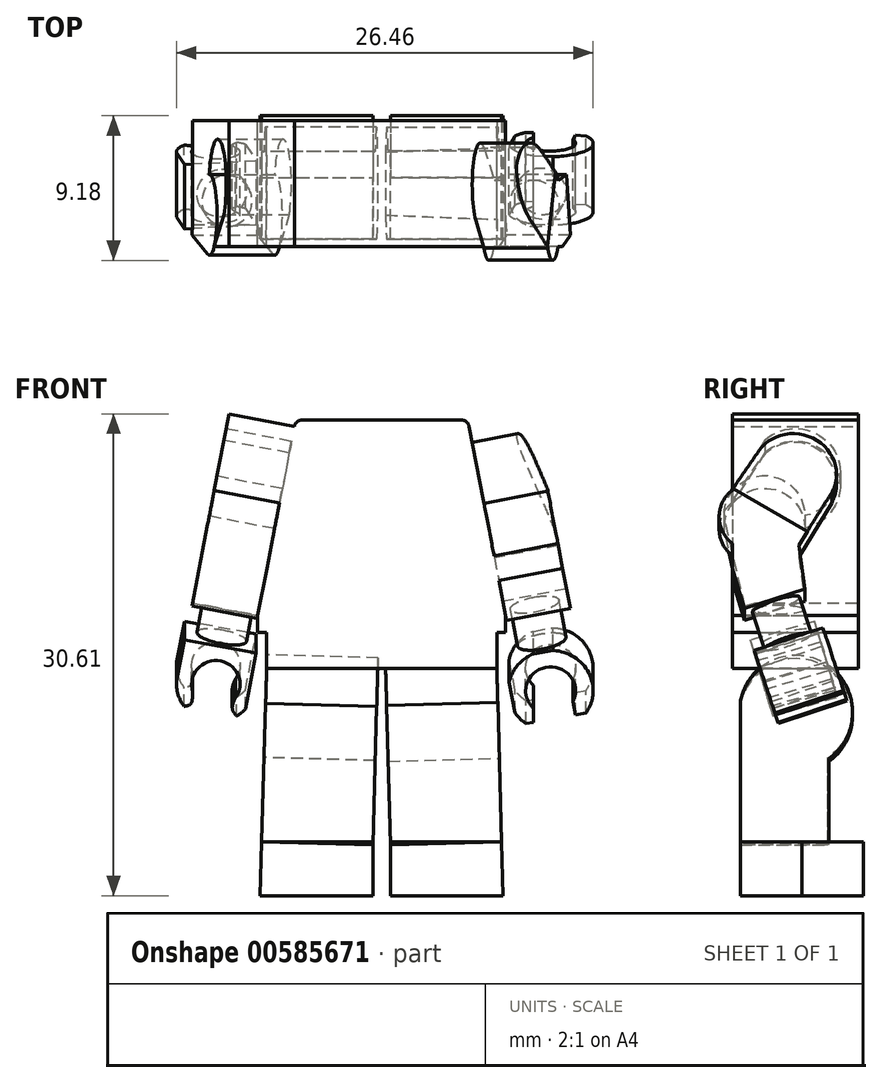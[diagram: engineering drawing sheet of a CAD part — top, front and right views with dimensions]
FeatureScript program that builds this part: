
annotation { "Feature Type Name" : "Feature", "Feature Type Description" : "" }
export const myFeature = defineFeature(function(context is Context, id is Id, definition is map)
    precondition{}
    {
        {
            var Q0;
            Q0=qCreatedBy(makeId("Front.planeOp"),FACE);
            var sketch = newSketch(context, id + "F0", { "sketchPlane" : qUnion([Q0])});
            skLineSegment(sketch, "E0", {"start": v(0, 25.85) * mm, "end": v(-2.45, 25.85) * mm});
            skLineSegment(sketch, "E1", {"start": v(-2.45, 25.85) * mm, "end": v(-2.45, 23.62) * mm});
            skLineSegment(sketch, "E2", {"start": v(-2.45, 23.62) * mm, "end": v(-3.1, 23.62) * mm});
            skLineSegment(sketch, "E3", {"start": v(-5.1, 21.62) * mm, "end": v(-5.1, 17.12) * mm});
            skLineSegment(sketch, "E4", {"start": v(-3.1, 15.12) * mm, "end": v(0, 15.12) * mm});
            skLineSegment(sketch, "E5", {"start": v(0, 25.85) * mm, "end": v(0, 15.12) * mm, "construction": true});
            skPoint(sketch, "E6.visualSharp", {"position": v(-5.1, 23.62) * mm});
            skArc(sketch, "E6.filletArc", {"start": v(-3.1, 23.62) * mm, "mid": v(-4.51, 23.03) * mm, "end": v(-5.1, 21.62) * mm});
            skPoint(sketch, "E7.visualSharp", {"position": v(-5.1, 15.12) * mm});
            skArc(sketch, "E7.filletArc", {"start": v(-5.1, 17.12) * mm, "mid": v(-4.51, 15.7) * mm, "end": v(-3.1, 15.12) * mm});
            skLineSegment(sketch, "E8", {"start": v(-3.1, 15.12) * mm, "end": v(-3.1, 14.02) * mm});
            skLineSegment(sketch, "E9", {"start": v(-3.1, 14.02) * mm, "end": v(0, 14.02) * mm});
            skLineSegment(sketch, "E10", {"start": v(0, 15.12) * mm, "end": v(0, 14.02) * mm, "construction": true});
            skLineSegment(sketch, "E11", {"start": v(0, 14.02) * mm, "end": v(-5.06, 14.02) * mm});
            skPoint(sketch, "E11.endSnap0", {"position": v(-1.55, 14.02) * mm});
            skLineSegment(sketch, "E12", {"start": v(-5.55, 13.62) * mm, "end": v(-7.87, 1.6) * mm});
            skLineSegment(sketch, "E13", {"start": v(-7.87, 1.6) * mm, "end": v(0, 1.6) * mm});
            skLineSegment(sketch, "E14", {"start": v(0, 14.02) * mm, "end": v(0, 1.6) * mm, "construction": true});
            skLineSegment(sketch, "E15.MirrorCS", {"start": v(5.55, 13.62) * mm, "end": v(7.87, 1.6) * mm});
            skLineSegment(sketch, "E16.MirrorCS", {"start": v(7.87, 1.6) * mm, "end": v(0, 1.6) * mm});
            skLineSegment(sketch, "E17.MirrorCS", {"start": v(0, 14.02) * mm, "end": v(5.06, 14.02) * mm});
            skLineSegment(sketch, "E18", {"start": v(-7.87, 1.6) * mm, "end": v(-7.87, 0.52) * mm});
            skLineSegment(sketch, "E19", {"start": v(-7.87, 0.52) * mm, "end": v(0, 0.52) * mm});
            skLineSegment(sketch, "E20", {"start": v(0, -31.62) * mm, "end": v(0, 1.6) * mm, "construction": true});
            skLineSegment(sketch, "E21", {"start": v(-7.3, 0.52) * mm, "end": v(-7.3, -1.76) * mm});
            skLineSegment(sketch, "E22", {"start": v(-7.3, -1.76) * mm, "end": v(0, -1.76) * mm});
            skLineSegment(sketch, "E23", {"start": v(-7.3, -1.76) * mm, "end": v(-7.72, -16.2) * mm});
            skLineSegment(sketch, "E24", {"start": v(-7.72, -16.2) * mm, "end": v(-0.56, -16.2) * mm});
            skLineSegment(sketch, "E25", {"start": v(-0.56, -16.2) * mm, "end": v(-0.56, -8.11) * mm});
            skLineSegment(sketch, "E26", {"start": v(-0.56, -8.11) * mm, "end": v(-0.85, -8.11) * mm});
            skLineSegment(sketch, "E27", {"start": v(-0.85, -8.11) * mm, "end": v(-0.85, -4.94) * mm});
            skLineSegment(sketch, "E28", {"start": v(-0.56, -8.11) * mm, "end": v(0, -8.11) * mm});
            skLineSegment(sketch, "E29.MirrorCS", {"start": v(7.87, 1.6) * mm, "end": v(7.87, 0.52) * mm});
            skLineSegment(sketch, "E30.MirrorCS", {"start": v(7.87, 0.52) * mm, "end": v(0, 0.52) * mm});
            skLineSegment(sketch, "E31.MirrorCS", {"start": v(7.3, -1.76) * mm, "end": v(0, -1.76) * mm});
            skLineSegment(sketch, "E32.MirrorCS", {"start": v(7.3, 0.52) * mm, "end": v(7.3, -1.76) * mm});
            skLineSegment(sketch, "E33.MirrorCS", {"start": v(0.85, -8.11) * mm, "end": v(0.85, -4.94) * mm});
            skLineSegment(sketch, "E34.MirrorCS", {"start": v(0.56, -8.11) * mm, "end": v(0.85, -8.11) * mm});
            skLineSegment(sketch, "E35.MirrorCS", {"start": v(0.56, -8.11) * mm, "end": v(0, -8.11) * mm});
            skLineSegment(sketch, "E36.MirrorCS", {"start": v(0.56, -16.2) * mm, "end": v(0.56, -8.11) * mm});
            skLineSegment(sketch, "E37.MirrorCS", {"start": v(7.72, -16.2) * mm, "end": v(0.56, -16.2) * mm});
            skLineSegment(sketch, "E38.MirrorCS", {"start": v(7.3, -1.76) * mm, "end": v(7.72, -16.2) * mm});
            skLineSegment(sketch, "E39", {"start": v(-7.62, -12.78) * mm, "end": v(-0.56, -12.78) * mm});
            skLineSegment(sketch, "E40", {"start": v(0.56, -12.78) * mm, "end": v(7.62, -12.78) * mm});
            skPoint(sketch, "E41", {"position": v(-0.85, -4.94) * mm});
            skLineSegment(sketch, "E42", {"start": v(-0.85, -4.94) * mm, "end": v(0, -4.94) * mm, "construction": true});
            skLineSegment(sketch, "E43", {"start": v(-0.85, -4.94) * mm, "end": v(-0.85, -1.76) * mm});
            skLineSegment(sketch, "E44", {"start": v(0, -4.94) * mm, "end": v(0.85, -4.94) * mm, "construction": true});
            skPoint(sketch, "E45", {"position": v(0.85, -4.94) * mm});
            skLineSegment(sketch, "E46", {"start": v(0.85, -4.94) * mm, "end": v(0.85, -1.76) * mm});
            skPoint(sketch, "E47.visualSharp", {"position": v(5.47, 14.02) * mm});
            skArc(sketch, "E47.filletArc", {"start": v(5.55, 13.62) * mm, "mid": v(5.38, 13.91) * mm, "end": v(5.06, 14.02) * mm});
            skPoint(sketch, "E48.visualSharp", {"position": v(-5.47, 14.02) * mm});
            skArc(sketch, "E48.filletArc", {"start": v(-5.06, 14.02) * mm, "mid": v(-5.38, 13.91) * mm, "end": v(-5.55, 13.62) * mm});
            skSolve(sketch);
        }
        {
            var Q0;
            Q0=sQuery(id+"F0.wireOp",EDGE,"E0");
            var Q1;
            Q1=sQuery(id+"F0.wireOp",EDGE,"E1");
            var Q2;
            Q2=sQuery(id+"F0.wireOp",EDGE,"E2");
            var Q3;
            Q3=sQuery(id+"F0.wireOp",EDGE,"E6.filletArc");
            var Q4;
            Q4=sQuery(id+"F0.wireOp",EDGE,"E3");
            var Q5;
            Q5=sQuery(id+"F0.wireOp",EDGE,"E7.filletArc");
            var Q6;
            Q6=sQuery(id+"F0.wireOp",EDGE,"E8");
            var Q7;
            Q7=sQuery(id+"F0.wireOp",EDGE,"E9");
            var Q8;
            Q8=sQuery(id+"F0.wireOp",EDGE,"E5");
            revolve(context, id + "F1", {"bodyType" : ToolBodyType.SURFACE, "surfaceEntities" : qUnion([Q0, Q1, Q2, Q3, Q4, Q5, Q6, Q7]), "axis" : qUnion([Q8]), "revolveType" : RevolveType.FULL});
        }
        {
            var Q0;
            {var subQ0=sQuery(id+"F0.wireOp",EDGE,"E24");Q0=makeQuery(id+"F0.imprint","IMPRINT",FACE,{"disambiguationData":[TD([[makeQuery(id+"F0.imprint","IMPRINT",EDGE,{"derivedFrom":subQ0}),1.0]])]});}
            var Q1;
            {var subQ0=sQuery(id+"F0.wireOp",EDGE,"E37.MirrorCS");Q1=makeQuery(id+"F0.imprint","IMPRINT",FACE,{"disambiguationData":[TD([[makeQuery(id+"F0.imprint","IMPRINT",EDGE,{"derivedFrom":subQ0}),-1.0]])]});}
            extrude(context, id + "F2", {"entities" : qUnion([Q0, Q1]), "depth" : 3.92 * mm, "offsetDistance" : 25 * mm});
        }
        {
            var Q0;
            {var subQ0=sQuery(id+"F0.wireOp",EDGE,"E24");Q0=makeQuery(id+"F0.imprint","IMPRINT",FACE,{"disambiguationData":[TD([[makeQuery(id+"F0.imprint","IMPRINT",EDGE,{"derivedFrom":subQ0}),1.0]])]});}
            var Q1;
            {var subQ0=sQuery(id+"F0.wireOp",EDGE,"E37.MirrorCS");Q1=makeQuery(id+"F0.imprint","IMPRINT",FACE,{"disambiguationData":[TD([[makeQuery(id+"F0.imprint","IMPRINT",EDGE,{"derivedFrom":subQ0}),-1.0]])]});}
            extrude(context, id + "F3", {"entities" : qUnion([Q0, Q1]), "oppositeDirection" : true, "depth" : 3.92 * mm, "offsetDistance" : 25 * mm});
        }
        {
            var Q0;
            Q0=makeQuery(id+"F2.opExtrude","SWEPT_FACE",FACE,{"disambiguationData":[OSD([sQuery(id+"F0.wireOp",EDGE,"E38.MirrorCS")])]});
            var sketch = newSketch(context, id + "F4", { "sketchPlane" : qUnion([Q0])});
            skLineSegment(sketch, "E49", {"start": v(-3.92, -12.99) * mm, "end": v(-3.92, -4.1) * mm});
            skLineSegment(sketch, "E50", {"start": v(-3.92, -4.1) * mm, "end": v(1.72, -12.99) * mm});
            skLineSegment(sketch, "E51", {"start": v(1.72, -12.99) * mm, "end": v(1.72, -7.67) * mm});
            skCircle(sketch, "E52", {"center": v(-0.38, -4.75) * mm, "radius": 3.6 * mm});
            skPoint(sketch, "E52.third.point", {"position": v(1.85, -1.94) * mm});
            skLineSegment(sketch, "E53", {"start": v(-3.92, -12.99) * mm, "end": v(1.72, -12.99) * mm});
            skSolve(sketch);
        }
        {
            var Q0;
            {var subQ3=sQuery(id+"F4.wireOp",EDGE,"E49");var subQ5=sQuery(id+"F4.wireOp",EDGE,"E52");var subQ6=makeQuery(id+"F4.imprint","INTERSECT",VERTEX,{"derivedFrom":[subQ3,subQ5]});Q0=makeQuery(id+"F4.imprint","IMPRINT",FACE,{"disambiguationData":[TD([[makeQuery(id+"F4.imprint","IMPRINT",EDGE,{"disambiguationData":[TD([[subQ6,-1.0]])],"derivedFrom":subQ5}),-1.0]])]});}
            var Q1;
            {var subQ0=sQuery(id+"F4.wireOp",EDGE,"E51");Q1=makeQuery(id+"F4.imprint","IMPRINT",FACE,{"disambiguationData":[TD([[makeQuery(id+"F4.imprint","IMPRINT",EDGE,{"derivedFrom":subQ0}),1.0]])]});}
            var Q2;
            {var subQ0=sQuery(id+"F4.wireOp",EDGE,"E52");var subQ2=sQuery(id+"F4.wireOp",EDGE,"E49");var subQ4=makeQuery(id+"F4.imprint","INTERSECT",VERTEX,{"derivedFrom":[subQ2,subQ0]});Q2=makeQuery(id+"F4.imprint","IMPRINT",FACE,{"disambiguationData":[TD([[makeQuery(id+"F4.imprint","IMPRINT",EDGE,{"disambiguationData":[TD([[subQ4,-1.0]])],"derivedFrom":subQ0}),1.0]])]});}
            var Q3;
            {var subQ0=sQuery(id+"F4.wireOp",EDGE,"E52");var subQ4=makeQuery(id+"F4.imprint","INTERSECT",VERTEX,{"derivedFrom":[sQuery(id+"F4.wireOp",EDGE,"E51"),subQ0]});Q3=makeQuery(id+"F4.imprint","IMPRINT",FACE,{"disambiguationData":[TD([[makeQuery(id+"F4.imprint","IMPRINT",EDGE,{"disambiguationData":[TD([[subQ4,1.0]])],"derivedFrom":subQ0}),1.0]])]});}
            extrude(context, id + "F5", {"entities" : qUnion([Q0, Q1, Q2, Q3]), "oppositeDirection" : true, "depth" : 7.06 * mm, "offsetDistance" : 25 * mm});
        }
        {
            var Q0;
            {var subQ0=sQuery(id+"F0.wireOp",EDGE,"E12");Q0=makeQuery(id+"F0.imprint","IMPRINT",FACE,{"disambiguationData":[TD([[makeQuery(id+"F0.imprint","IMPRINT",EDGE,{"derivedFrom":subQ0}),1.0]])]});}
            var Q1;
            Q1=makeQuery(id+"F0.imprint","IMPRINT",FACE,{"disambiguationData":[TD([[makeQuery(id+"F0.imprint","IMPRINT",EDGE,{"derivedFrom":sQuery(id+"F0.wireOp",EDGE,"E13")}),-1.0]])]});
            var Q2;
            {var subQ8=sQuery(id+"F0.wireOp",EDGE,"E21");Q2=makeQuery(id+"F0.imprint","IMPRINT",FACE,{"disambiguationData":[TD([[makeQuery(id+"F0.imprint","IMPRINT",EDGE,{"derivedFrom":subQ8}),1.0]])]});}
            extrude(context, id + "F6", {"entities" : qUnion([Q0, Q1, Q2]), "operationType" : NewBodyOperationType.ADD, "depth" : 4.4 * mm, "offsetDistance" : 25 * mm});
        }
        {
            var Q0;
            {var subQ8=sQuery(id+"F0.wireOp",EDGE,"E21");Q0=makeQuery(id+"F0.imprint","IMPRINT",FACE,{"disambiguationData":[TD([[makeQuery(id+"F0.imprint","IMPRINT",EDGE,{"derivedFrom":subQ8}),1.0]])]});}
            var Q1;
            Q1=makeQuery(id+"F0.imprint","IMPRINT",FACE,{"disambiguationData":[TD([[makeQuery(id+"F0.imprint","IMPRINT",EDGE,{"derivedFrom":sQuery(id+"F0.wireOp",EDGE,"E13")}),-1.0]])]});
            var Q2;
            {var subQ0=sQuery(id+"F0.wireOp",EDGE,"E12");Q2=makeQuery(id+"F0.imprint","IMPRINT",FACE,{"disambiguationData":[TD([[makeQuery(id+"F0.imprint","IMPRINT",EDGE,{"derivedFrom":subQ0}),1.0]])]});}
            extrude(context, id + "F7", {"entities" : qUnion([Q0, Q1, Q2]), "operationType" : NewBodyOperationType.ADD, "oppositeDirection" : true, "depth" : 3.6 * mm, "offsetDistance" : 25 * mm});
        }
        {
            var Q0;
            Q0=sQuery(id+"F0.wireOp",EDGE,"E27");
            var Q1;
            Q1=sQuery(id+"F0.wireOp",EDGE,"E26");
            var Q2;
            Q2=sQuery(id+"F0.wireOp",EDGE,"E28");
            var Q3;
            Q3=sQuery(id+"F0.wireOp",EDGE,"E42");
            revolve(context, id + "F8", {"bodyType" : ToolBodyType.SURFACE, "surfaceEntities" : qUnion([Q0, Q1, Q2]), "axis" : qUnion([Q3]), "revolveType" : RevolveType.FULL});
        }
        {
            var Q0;
            Q0=sQuery(id+"F0.wireOp",EDGE,"E33.MirrorCS");
            var Q1;
            Q1=sQuery(id+"F0.wireOp",EDGE,"E34.MirrorCS");
            var Q2;
            Q2=sQuery(id+"F0.wireOp",EDGE,"E35.MirrorCS");
            var Q3;
            Q3=sQuery(id+"F0.wireOp",EDGE,"E44");
            revolve(context, id + "F9", {"bodyType" : ToolBodyType.SURFACE, "surfaceEntities" : qUnion([Q0, Q1, Q2]), "axis" : qUnion([Q3]), "revolveType" : RevolveType.FULL});
        }
        {
            var Q0;
            Q0=makeQuery(id+"F2.opExtrude","SWEPT_FACE",FACE,{"disambiguationData":[OSD([sQuery(id+"F0.wireOp",EDGE,"E23")])]});
            var sketch = newSketch(context, id + "F10", { "sketchPlane" : qUnion([Q0])});
            skLineSegment(sketch, "E54", {"start": v(3.92, -12.99) * mm, "end": v(3.92, -4.17) * mm});
            skLineSegment(sketch, "E55", {"start": v(3.92, -4.17) * mm, "end": v(-1.65, -12.99) * mm});
            skLineSegment(sketch, "E56", {"start": v(-1.65, -12.99) * mm, "end": v(-1.65, -7.62) * mm});
            skLineSegment(sketch, "E57", {"start": v(-1.65, -7.62) * mm, "end": v(3.92, -12.99) * mm});
            skCircle(sketch, "E58", {"center": v(0.38, -4.67) * mm, "radius": 3.57 * mm});
            skPoint(sketch, "E58.third.point", {"position": v(-2.76, -2.98) * mm});
            skLineSegment(sketch, "E59", {"start": v(-1.65, -12.99) * mm, "end": v(3.92, -12.99) * mm});
            skSolve(sketch);
        }
        {
            var Q0;
            {var subQ1=sQuery(id+"F10.wireOp",EDGE,"E55");var subQ3=sQuery(id+"F10.wireOp",EDGE,"E57");var subQ4=makeQuery(id+"F10.imprint","INTERSECT",VERTEX,{"derivedFrom":[subQ1,subQ3]});Q0=makeQuery(id+"F10.imprint","IMPRINT",FACE,{"disambiguationData":[TD([[makeQuery(id+"F10.imprint","IMPRINT",EDGE,{"disambiguationData":[TD([[subQ4,-1.0]])],"derivedFrom":subQ1}),1.0]])]});}
            var Q1;
            {var subQ0=sQuery(id+"F10.wireOp",EDGE,"E56");Q1=makeQuery(id+"F10.imprint","IMPRINT",FACE,{"disambiguationData":[TD([[makeQuery(id+"F10.imprint","IMPRINT",EDGE,{"derivedFrom":subQ0}),-1.0]])]});}
            var Q2;
            {var subQ3=sQuery(id+"F10.wireOp",EDGE,"E58");var subQ5=sQuery(id+"F10.wireOp",EDGE,"E55");var subQ6=makeQuery(id+"F10.imprint","INTERSECT",VERTEX,{"derivedFrom":[subQ5,subQ3]});Q2=makeQuery(id+"F10.imprint","IMPRINT",FACE,{"disambiguationData":[TD([[makeQuery(id+"F10.imprint","IMPRINT",EDGE,{"disambiguationData":[TD([[subQ6,-1.0]])],"derivedFrom":subQ5}),1.0]])]});}
            var Q3;
            {var subQ0=sQuery(id+"F10.wireOp",EDGE,"E58");var subQ1=sQuery(id+"F10.wireOp",EDGE,"E55");var subQ3=makeQuery(id+"F10.imprint","INTERSECT",VERTEX,{"derivedFrom":[subQ1,subQ0]});Q3=makeQuery(id+"F10.imprint","IMPRINT",FACE,{"disambiguationData":[TD([[makeQuery(id+"F10.imprint","IMPRINT",EDGE,{"disambiguationData":[TD([[subQ3,1.0]])],"derivedFrom":subQ1}),-1.0]])]});}
            var Q4;
            {var subQ0=sQuery(id+"F10.wireOp",EDGE,"E58");var subQ2=sQuery(id+"F10.wireOp",EDGE,"E54");var subQ4=makeQuery(id+"F10.imprint","INTERSECT",VERTEX,{"derivedFrom":[subQ2,subQ0]});Q4=makeQuery(id+"F10.imprint","IMPRINT",FACE,{"disambiguationData":[TD([[makeQuery(id+"F10.imprint","IMPRINT",EDGE,{"disambiguationData":[TD([[subQ4,1.0]])],"derivedFrom":subQ0}),1.0]])]});}
            var Q5;
            {var subQ0=sQuery(id+"F10.wireOp",EDGE,"E58");var subQ1=sQuery(id+"F10.wireOp",EDGE,"E55");var subQ2=makeQuery(id+"F10.imprint","INTERSECT",VERTEX,{"derivedFrom":[subQ1,subQ0]});Q5=makeQuery(id+"F10.imprint","IMPRINT",FACE,{"disambiguationData":[TD([[makeQuery(id+"F10.imprint","IMPRINT",EDGE,{"disambiguationData":[TD([[subQ2,-1.0]])],"derivedFrom":subQ1}),-1.0]])]});}
            extrude(context, id + "F11", {"entities" : qUnion([Q0, Q1, Q2, Q3, Q4, Q5]), "oppositeDirection" : true, "depth" : 7.06 * mm, "offsetDistance" : 25 * mm});
        }
        {
            var Q0;
            {var subQ0=sQuery(id+"F0.wireOp",EDGE,"E15.MirrorCS");Q0=makeQuery(id+"F7.boolean.opBoolean","MERGE",FACE,{"derivedFrom":[makeQuery(id+"F6.opExtrude","SWEPT_FACE",FACE,{"disambiguationData":[OSD([subQ0])]}),makeQuery(id+"F7.opExtrude","SWEPT_FACE",FACE,{"disambiguationData":[OSD([subQ0])]})]});}
            var sketch = newSketch(context, id + "F12", { "sketchPlane" : qUnion([Q0])});
            skCircle(sketch, "E60", {"center": v(-0.48, 8.6) * mm, "radius": 2.68 * mm});
            skCircle(sketch, "E61", {"center": v(-3.08, 5.68) * mm, "radius": 2.18 * mm});
            skPoint(sketch, "E61.first.point", {"position": v(-5.17, 6.3) * mm});
            skPoint(sketch, "E61.second.point", {"position": v(-1.1, 4.76) * mm});
            skPoint(sketch, "E61.third.point", {"position": v(-1.39, 7.07) * mm});
            skLineSegment(sketch, "E62", {"start": v(-5.17, 6.3) * mm, "end": v(-2.73, 10.06) * mm});
            skLineSegment(sketch, "E63", {"start": v(-2.73, 10.06) * mm, "end": v(1.9, 7.38) * mm});
            skLineSegment(sketch, "E64", {"start": v(1.9, 7.38) * mm, "end": v(-0.2, 3.82) * mm});
            skLineSegment(sketch, "E65", {"start": v(-0.2, 3.82) * mm, "end": v(0.18, 1) * mm});
            skLineSegment(sketch, "E66", {"start": v(0.18, 1) * mm, "end": v(-3.67, -0.24) * mm});
            skLineSegment(sketch, "E67", {"start": v(-3.67, -0.24) * mm, "end": v(-5.17, 5.07) * mm});
            skSolve(sketch);
        }
        {
            var Q0;
            {var subQ0=sQuery(id+"F12.wireOp",EDGE,"E63");Q0=makeQuery(id+"F12.imprint","IMPRINT",FACE,{"disambiguationData":[TD([[makeQuery(id+"F12.imprint","IMPRINT",EDGE,{"derivedFrom":subQ0}),1.0]])]});}
            var Q1;
            {var subQ5=sQuery(id+"F12.wireOp",EDGE,"E63");Q1=makeQuery(id+"F12.imprint","IMPRINT",FACE,{"disambiguationData":[TD([[makeQuery(id+"F12.imprint","IMPRINT",EDGE,{"derivedFrom":subQ5}),-1.0]])]});}
            var Q2;
            {var subQ0=sQuery(id+"F12.wireOp",EDGE,"E61");var subQ1=sQuery(id+"F12.wireOp",EDGE,"E60");var subQ2=makeQuery(id+"F12.imprint","INTERSECT",VERTEX,{"disambiguationData":[OD(0.0)],"derivedFrom":[subQ1,subQ0]});Q2=makeQuery(id+"F12.imprint","IMPRINT",FACE,{"disambiguationData":[TD([[makeQuery(id+"F12.imprint","IMPRINT",EDGE,{"disambiguationData":[TD([[subQ2,-1.0]])],"derivedFrom":subQ1}),1.0]])]});}
            var Q3;
            {var subQ1=sQuery(id+"F12.wireOp",EDGE,"E60");var subQ3=sQuery(id+"F12.wireOp",EDGE,"E61");var subQ4=makeQuery(id+"F12.imprint","INTERSECT",VERTEX,{"disambiguationData":[OD(0.0)],"derivedFrom":[subQ1,subQ3]});Q3=makeQuery(id+"F12.imprint","IMPRINT",FACE,{"disambiguationData":[TD([[makeQuery(id+"F12.imprint","IMPRINT",EDGE,{"disambiguationData":[TD([[subQ4,-1.0]])],"derivedFrom":subQ3}),-1.0]])]});}
            var Q4;
            {var subQ0=sQuery(id+"F12.wireOp",EDGE,"E61");var subQ1=sQuery(id+"F12.wireOp",EDGE,"E60");var subQ2=makeQuery(id+"F12.imprint","INTERSECT",VERTEX,{"disambiguationData":[OD(0.0)],"derivedFrom":[subQ1,subQ0]});Q4=makeQuery(id+"F12.imprint","IMPRINT",FACE,{"disambiguationData":[TD([[makeQuery(id+"F12.imprint","IMPRINT",EDGE,{"disambiguationData":[TD([[subQ2,-1.0]])],"derivedFrom":subQ1}),-1.0]])]});}
            var Q5;
            {var subQ0=sQuery(id+"F12.wireOp",EDGE,"E65");Q5=makeQuery(id+"F12.imprint","IMPRINT",FACE,{"disambiguationData":[TD([[makeQuery(id+"F12.imprint","IMPRINT",EDGE,{"derivedFrom":subQ0}),-1.0]])]});}
            var Q6;
            {var subQ0=sQuery(id+"F12.wireOp",EDGE,"E67");var subQ1=sQuery(id+"F12.wireOp",EDGE,"E61");var subQ2=makeQuery(id+"F12.imprint","INTERSECT",VERTEX,{"derivedFrom":[subQ1,subQ0]});Q6=makeQuery(id+"F12.imprint","IMPRINT",FACE,{"disambiguationData":[TD([[makeQuery(id+"F12.imprint","IMPRINT",EDGE,{"disambiguationData":[TD([[subQ2,-1.0]])],"derivedFrom":subQ1}),-1.0]])]});}
            var Q7;
            {var subQ0=sQuery(id+"F12.wireOp",EDGE,"E61");var subQ4=sQuery(id+"F12.wireOp",EDGE,"E62");var subQ6=makeQuery(id+"F12.imprint","INTERSECT",VERTEX,{"disambiguationData":[OD(1.0)],"derivedFrom":[subQ0,subQ4]});Q7=makeQuery(id+"F12.imprint","IMPRINT",FACE,{"disambiguationData":[TD([[makeQuery(id+"F12.imprint","IMPRINT",EDGE,{"disambiguationData":[TD([[subQ6,1.0]])],"derivedFrom":subQ0}),1.0]])]});}
            var Q8;
            {var subQ0=sQuery(id+"F12.wireOp",EDGE,"E62");var subQ1=sQuery(id+"F12.wireOp",EDGE,"E61");var subQ2=makeQuery(id+"F12.imprint","INTERSECT",VERTEX,{"disambiguationData":[OD(0.0)],"derivedFrom":[subQ1,subQ0]});Q8=makeQuery(id+"F12.imprint","IMPRINT",FACE,{"disambiguationData":[TD([[makeQuery(id+"F12.imprint","IMPRINT",EDGE,{"disambiguationData":[TD([[subQ2,1.0]])],"derivedFrom":subQ1}),1.0]])]});}
            var Q9;
            {var subQ0=sQuery(id+"F12.wireOp",EDGE,"E62");var subQ1=sQuery(id+"F12.wireOp",EDGE,"E61");var subQ2=makeQuery(id+"F12.imprint","INTERSECT",VERTEX,{"disambiguationData":[OD(1.0)],"derivedFrom":[subQ1,subQ0]});Q9=makeQuery(id+"F12.imprint","IMPRINT",FACE,{"disambiguationData":[TD([[makeQuery(id+"F12.imprint","IMPRINT",EDGE,{"disambiguationData":[TD([[subQ2,1.0]])],"derivedFrom":subQ1}),-1.0]])]});}
            var Q10;
            {var subQ0=sQuery(id+"F12.wireOp",EDGE,"E67");var subQ1=sQuery(id+"F12.wireOp",EDGE,"E66");var subQ2=makeQuery(id+"F12.imprint","INTERSECT",VERTEX,{"derivedFrom":[subQ1,subQ0]});Q10=makeQuery(id+"F12.imprint","IMPRINT",FACE,{"disambiguationData":[TD([[makeQuery(id+"F12.imprint","IMPRINT",EDGE,{"disambiguationData":[TD([[subQ2,1.0]])],"derivedFrom":subQ1}),-1.0]])]});}
            extrude(context, id + "F13", {"entities" : qUnion([Q0, Q1, Q2, Q3, Q4, Q5, Q6, Q7, Q8, Q9, Q10]), "operationType" : NewBodyOperationType.ADD, "depth" : 4.13 * mm, "offsetDistance" : 25 * mm});
        }
        {
            var Q0;
            {var subQ0=sQuery(id+"F0.wireOp",EDGE,"E12");Q0=makeQuery(id+"F7.boolean.opBoolean","MERGE",FACE,{"derivedFrom":[makeQuery(id+"F6.opExtrude","SWEPT_FACE",FACE,{"disambiguationData":[OSD([subQ0])]}),makeQuery(id+"F7.opExtrude","SWEPT_FACE",FACE,{"disambiguationData":[OSD([subQ0])]})]});}
            var sketch = newSketch(context, id + "F14", { "sketchPlane" : qUnion([Q0])});
            skCircle(sketch, "E68", {"center": v(0.42, 8.52) * mm, "radius": 2.85 * mm});
            skCircle(sketch, "E69", {"center": v(2.38, 5.77) * mm, "radius": 2.56 * mm});
            skPoint(sketch, "E69.first.point", {"position": v(4.94, 5.75) * mm});
            skPoint(sketch, "E69.second.point", {"position": v(-0.15, 5.4) * mm});
            skPoint(sketch, "E69.third.point", {"position": v(0.35, 7.31) * mm});
            skLineSegment(sketch, "E70", {"start": v(2.34, 10.63) * mm, "end": v(4.54, 7.13) * mm});
            skLineSegment(sketch, "E71", {"start": v(4.54, 7.13) * mm, "end": v(4.87, 5.2) * mm});
            skLineSegment(sketch, "E72", {"start": v(4.87, 5.2) * mm, "end": v(3.65, -0.11) * mm});
            skLineSegment(sketch, "E73", {"start": v(3.65, -0.11) * mm, "end": v(-0.4, 1.06) * mm});
            skLineSegment(sketch, "E74", {"start": v(-0.4, 1.06) * mm, "end": v(0.17, 3.92) * mm});
            skLineSegment(sketch, "E75", {"start": v(0.17, 3.92) * mm, "end": v(-1.92, 6.88) * mm});
            skSolve(sketch);
        }
        {
            var Q0;
            {var subQ0=sQuery(id+"F14.wireOp",EDGE,"E70");var subQ1=sQuery(id+"F14.wireOp",EDGE,"E68");var subQ7=makeQuery(id+"F14.imprint","INTERSECT",VERTEX,{"disambiguationData":[OD(0.0)],"derivedFrom":[subQ1,subQ0]});Q0=makeQuery(id+"F14.imprint","IMPRINT",FACE,{"disambiguationData":[TD([[makeQuery(id+"F14.imprint","IMPRINT",EDGE,{"disambiguationData":[TD([[subQ7,-1.0]])],"derivedFrom":subQ1}),1.0]])]});}
            var Q1;
            {var subQ0=sQuery(id+"F14.wireOp",EDGE,"E69");var subQ1=sQuery(id+"F14.wireOp",EDGE,"E68");var subQ2=makeQuery(id+"F14.imprint","INTERSECT",VERTEX,{"disambiguationData":[OD(0.0)],"derivedFrom":[subQ1,subQ0]});Q1=makeQuery(id+"F14.imprint","IMPRINT",FACE,{"disambiguationData":[TD([[makeQuery(id+"F14.imprint","IMPRINT",EDGE,{"disambiguationData":[TD([[subQ2,-1.0]])],"derivedFrom":subQ1}),1.0]])]});}
            var Q2;
            {var subQ0=sQuery(id+"F14.wireOp",EDGE,"E69");var subQ1=sQuery(id+"F14.wireOp",EDGE,"E68");var subQ2=makeQuery(id+"F14.imprint","INTERSECT",VERTEX,{"disambiguationData":[OD(0.0)],"derivedFrom":[subQ1,subQ0]});Q2=makeQuery(id+"F14.imprint","IMPRINT",FACE,{"disambiguationData":[TD([[makeQuery(id+"F14.imprint","IMPRINT",EDGE,{"disambiguationData":[TD([[subQ2,-1.0]])],"derivedFrom":subQ1}),-1.0]])]});}
            var Q3;
            {var subQ0=sQuery(id+"F14.wireOp",EDGE,"E74");Q3=makeQuery(id+"F14.imprint","IMPRINT",FACE,{"disambiguationData":[TD([[makeQuery(id+"F14.imprint","IMPRINT",EDGE,{"derivedFrom":subQ0}),-1.0]])]});}
            var Q4;
            {var subQ0=sQuery(id+"F14.wireOp",EDGE,"E73");var subQ1=sQuery(id+"F14.wireOp",EDGE,"E72");var subQ2=makeQuery(id+"F14.imprint","INTERSECT",VERTEX,{"derivedFrom":[subQ1,subQ0]});Q4=makeQuery(id+"F14.imprint","IMPRINT",FACE,{"disambiguationData":[TD([[makeQuery(id+"F14.imprint","IMPRINT",EDGE,{"disambiguationData":[TD([[subQ2,1.0]])],"derivedFrom":subQ1}),-1.0]])]});}
            var Q5;
            {var subQ0=sQuery(id+"F14.wireOp",EDGE,"E71");Q5=makeQuery(id+"F14.imprint","IMPRINT",FACE,{"disambiguationData":[TD([[makeQuery(id+"F14.imprint","IMPRINT",EDGE,{"derivedFrom":subQ0}),1.0]])]});}
            var Q6;
            {var subQ0=sQuery(id+"F14.wireOp",EDGE,"E71");Q6=makeQuery(id+"F14.imprint","IMPRINT",FACE,{"disambiguationData":[TD([[makeQuery(id+"F14.imprint","IMPRINT",EDGE,{"derivedFrom":subQ0}),-1.0]])]});}
            var Q7;
            {var subQ0=sQuery(id+"F14.wireOp",EDGE,"E70");var subQ1=sQuery(id+"F14.wireOp",EDGE,"E68");var subQ2=makeQuery(id+"F14.imprint","INTERSECT",VERTEX,{"disambiguationData":[OD(1.0)],"derivedFrom":[subQ1,subQ0]});Q7=makeQuery(id+"F14.imprint","IMPRINT",FACE,{"disambiguationData":[TD([[makeQuery(id+"F14.imprint","IMPRINT",EDGE,{"disambiguationData":[TD([[subQ2,1.0]])],"derivedFrom":subQ1}),-1.0]])]});}
            var Q8;
            {var subQ0=sQuery(id+"F14.wireOp",EDGE,"E72");var subQ3=makeQuery(id+"F6.opExtrude","CAP_EDGE",EDGE,{"disambiguationData":[OSD([sQuery(id+"F0.wireOp",EDGE,"E12")])],"isStart":false});var subQ5=makeQuery(id+"F14.imprint","INTERSECT",VERTEX,{"derivedFrom":[subQ3,subQ0]});Q8=makeQuery(id+"F14.imprint","IMPRINT",FACE,{"disambiguationData":[TD([[makeQuery(id+"F14.imprint","IMPRINT",EDGE,{"disambiguationData":[TD([[subQ5,1.0]])],"derivedFrom":subQ3}),1.0]])]});}
            extrude(context, id + "F15", {"entities" : qUnion([Q0, Q1, Q2, Q3, Q4, Q5, Q6, Q7, Q8]), "operationType" : NewBodyOperationType.ADD, "depth" : 4.22 * mm, "offsetDistance" : 25 * mm});
        }
        {
            var Q0;
            Q0=makeQuery(id+"F13.opExtrude","SWEPT_FACE",FACE,{"disambiguationData":[OSD([sQuery(id+"F12.wireOp",EDGE,"E66")])]});
            var sketch = newSketch(context, id + "F16", { "sketchPlane" : qUnion([Q0])});
            skCircle(sketch, "E76", {"center": v(10.04, 0.85) * mm, "radius": 1.57 * mm});
            skSolve(sketch);
        }
        {
            var Q0;
            Q0 = qSketchRegion(id + "F16", true);
            extrude(context, id + "F17", {"entities" : qUnion([Q0]), "operationType" : NewBodyOperationType.ADD, "depth" : 2.5 * mm, "offsetDistance" : 25 * mm});
        }
        {
            var Q0;
            Q0=makeQuery(id+"F17.opExtrude","CAP_FACE",FACE,{"disambiguationData":[OSD([sQuery(id+"F16.wireOp",EDGE,"E76")])],"isStart":false});
            var sketch = newSketch(context, id + "F18", { "sketchPlane" : qUnion([Q0])});
            skLineSegment(sketch, "E77.bottom", {"start": v(7.65, -1.52) * mm, "end": v(12.83, -1.52) * mm});
            skLineSegment(sketch, "E77.top", {"start": v(7.65, 3.07) * mm, "end": v(12.83, 3.07) * mm});
            skLineSegment(sketch, "E77.left", {"start": v(7.65, -1.52) * mm, "end": v(7.65, 3.07) * mm});
            skLineSegment(sketch, "E77.right", {"start": v(12.83, -1.52) * mm, "end": v(12.83, 3.07) * mm});
            skSolve(sketch);
        }
        {
            var Q0;
            Q0 = qSketchRegion(id + "F18", true);
            extrude(context, id + "F19", {"entities" : qUnion([Q0]), "operationType" : NewBodyOperationType.ADD, "depth" : 4.5 * mm, "offsetDistance" : 25 * mm});
        }
        {
            var Q0;
            Q0=makeQuery(id+"F19.opExtrude","SWEPT_FACE",FACE,{"disambiguationData":[OSD([sQuery(id+"F18.wireOp",EDGE,"E77.bottom")])]});
            var sketch = newSketch(context, id + "F20", { "sketchPlane" : qUnion([Q0])});
            skCircle(sketch, "E78", {"center": v(-10.73, -2.32) * mm, "radius": 2.7 * mm});
            skCircle(sketch, "E79", {"center": v(-10.73, -2.32) * mm, "radius": 1.6 * mm});
            skSolve(sketch);
        }
        {
            var Q0;
            {var subQ0=sQuery(id+"F18.wireOp",EDGE,"E77.bottom");var subQ5=makeQuery(id+"F19.opExtrude","CAP_EDGE",EDGE,{"disambiguationData":[OSD([subQ0])],"isStart":true});Q0=makeQuery(id+"F20.imprint","IMPRINT",FACE,{"disambiguationData":[TD([[makeQuery(id+"F20.imprint","IMPRINT",EDGE,{"derivedFrom":subQ5}),1.0]])]});}
            var Q1;
            {var subQ0=sQuery(id+"F20.wireOp",EDGE,"E78");var subQ1=sQuery(id+"F18.wireOp",EDGE,"E77.bottom");var subQ4=makeQuery(id+"F19.opExtrude","CAP_EDGE",EDGE,{"disambiguationData":[OSD([subQ1])],"isStart":false});var subQ5=makeQuery(id+"F20.imprint","INTERSECT",VERTEX,{"disambiguationData":[OD(0.0)],"derivedFrom":[subQ4,subQ0]});Q1=makeQuery(id+"F20.imprint","IMPRINT",FACE,{"disambiguationData":[TD([[makeQuery(id+"F20.imprint","IMPRINT",EDGE,{"disambiguationData":[TD([[subQ5,1.0]])],"derivedFrom":subQ0}),-1.0]])]});}
            var Q2;
            {var subQ0=sQuery(id+"F20.wireOp",EDGE,"E79");var subQ1=makeQuery(id+"F19.opExtrude","CAP_EDGE",EDGE,{"disambiguationData":[OSD([sQuery(id+"F18.wireOp",EDGE,"E77.bottom")])],"isStart":false});var subQ2=makeQuery(id+"F20.imprint","INTERSECT",VERTEX,{"disambiguationData":[OD(0.0)],"derivedFrom":[subQ1,subQ0]});Q2=makeQuery(id+"F20.imprint","IMPRINT",FACE,{"disambiguationData":[TD([[makeQuery(id+"F20.imprint","IMPRINT",EDGE,{"disambiguationData":[TD([[subQ2,1.0]])],"derivedFrom":subQ0}),1.0]])]});}
            var Q3;
            {var subQ0=sQuery(id+"F20.wireOp",EDGE,"E78");var subQ1=sQuery(id+"F18.wireOp",EDGE,"E77.bottom");var subQ2=makeQuery(id+"F19.opExtrude","CAP_EDGE",EDGE,{"disambiguationData":[OSD([subQ1])],"isStart":false});var subQ3=makeQuery(id+"F20.imprint","INTERSECT",VERTEX,{"disambiguationData":[OD(1.0)],"derivedFrom":[subQ2,subQ0]});Q3=makeQuery(id+"F20.imprint","IMPRINT",FACE,{"disambiguationData":[TD([[makeQuery(id+"F20.imprint","IMPRINT",EDGE,{"disambiguationData":[TD([[subQ3,-1.0]])],"derivedFrom":subQ0}),-1.0]])]});}
            extrude(context, id + "F21", {"entities" : qUnion([Q0, Q1, Q2, Q3]), "operationType" : NewBodyOperationType.REMOVE, "oppositeDirection" : true, "depth" : 25 * mm, "offsetDistance" : 25 * mm});
        }
        {
            var Q0;
            Q0=makeQuery(id+"F19.opExtrude","SWEPT_FACE",FACE,{"disambiguationData":[OSD([sQuery(id+"F18.wireOp",EDGE,"E77.bottom")])]});
            var sketch = newSketch(context, id + "F22", { "sketchPlane" : qUnion([Q0])});
            skCircle(sketch, "E80", {"center": v(-10.61, -2) * mm, "radius": 1.56 * mm});
            skLineSegment(sketch, "E81", {"start": v(-12.06, -2.56) * mm, "end": v(-12.32, -3.94) * mm});
            skLineSegment(sketch, "E82", {"start": v(-12.32, -3.94) * mm, "end": v(-9.63, -4.43) * mm});
            skLineSegment(sketch, "E83", {"start": v(-9.63, -4.43) * mm, "end": v(-9.63, -3.2) * mm});
            skSolve(sketch);
        }
        {
            var Q0;
            Q0=makeQuery(id+"F22.imprint","IMPRINT",FACE,{"disambiguationData":[TD([[makeQuery(id+"F22.imprint","IMPRINT",EDGE,{"derivedFrom":sQuery(id+"F22.wireOp",EDGE,"E80")}),1.0]])]});
            var Q1;
            {var subQ0=sQuery(id+"F22.wireOp",EDGE,"E81");Q1=makeQuery(id+"F22.imprint","IMPRINT",FACE,{"disambiguationData":[TD([[makeQuery(id+"F22.imprint","IMPRINT",EDGE,{"derivedFrom":subQ0}),1.0]])]});}
            extrude(context, id + "F23", {"entities" : qUnion([Q0, Q1]), "operationType" : NewBodyOperationType.REMOVE, "oppositeDirection" : true, "depth" : 25 * mm, "offsetDistance" : 25 * mm});
        }
        {
            var Q0;
            Q0=makeQuery(id+"F13.opExtrude","SWEPT_FACE",FACE,{"disambiguationData":[OSD([sQuery(id+"F12.wireOp",EDGE,"E64")])]});
            var sketch = newSketch(context, id + "F24", { "sketchPlane" : qUnion([Q0])});
            skFitSpline(sketch, "E84", {"points": [v(-11.3, 6.18) * mm, v(-8.83, 11.88) * mm, v(-7.6, 13.1) * mm, v(-7.32, 13.23) * mm], "startDerivative": vector(4.18, 11.73) * mm, "endDerivative": vector(1.92, 0.77) * mm});
            skLineSegment(sketch, "E85", {"start": v(-7.32, 13.23) * mm, "end": v(-10.04, 13.7) * mm});
            skLineSegment(sketch, "E86", {"start": v(-10.04, 13.7) * mm, "end": v(-11.3, 6.18) * mm});
            skSolve(sketch);
        }
        {
            var Q0;
            {var subQ0=sQuery(id+"F24.wireOp",EDGE,"E85");Q0=makeQuery(id+"F24.imprint","IMPRINT",FACE,{"disambiguationData":[TD([[makeQuery(id+"F24.imprint","IMPRINT",EDGE,{"derivedFrom":subQ0}),1.0]])]});}
            var Q1;
            {var subQ0=sQuery(id+"F24.wireOp",EDGE,"E86");var subQ1=sQuery(id+"F24.wireOp",EDGE,"E84");var subQ2=sQuery(id+"F12.wireOp",EDGE,"E64");var subQ3=makeQuery(id+"F24.imprint","INTERSECT",VERTEX,{"derivedFrom":[makeQuery(id+"F13.opExtrude","CAP_EDGE",EDGE,{"disambiguationData":[OSD([subQ2])],"isStart":false}),subQ1,subQ0]});Q1=makeQuery(id+"F24.imprint","IMPRINT",FACE,{"disambiguationData":[TD([[makeQuery(id+"F24.imprint","IMPRINT",EDGE,{"disambiguationData":[TD([[subQ3,-1.0]])],"derivedFrom":subQ1}),1.0]])]});}
            extrude(context, id + "F25", {"entities" : qUnion([Q0, Q1]), "operationType" : NewBodyOperationType.REMOVE, "oppositeDirection" : true, "depth" : 25 * mm, "offsetDistance" : 25 * mm});
        }
        {
            var Q0;
            Q0=makeQuery(id+"F15.opExtrude","SWEPT_FACE",FACE,{"disambiguationData":[OSD([sQuery(id+"F14.wireOp",EDGE,"E73")])]});
            var sketch = newSketch(context, id + "F26", { "sketchPlane" : qUnion([Q0])});
            skPoint(sketch, "E87", {"position": v(-10.1, 0.77) * mm});
            skPoint(sketch, "E87.positionSnap0", {"position": v(-10.1, -1.22) * mm});
            skPoint(sketch, "E87.positionSnap1", {"position": v(-12.31, 0.77) * mm});
            skCircle(sketch, "E88", {"center": v(-10.1, 0.88) * mm, "radius": 1.6 * mm});
            skSolve(sketch);
        }
        {
            var Q0;
            Q0=makeQuery(id+"F26.imprint","IMPRINT",FACE,{"disambiguationData":[TD([[makeQuery(id+"F26.imprint","IMPRINT",EDGE,{"derivedFrom":sQuery(id+"F26.wireOp",EDGE,"E88")}),1.0]])]});
            extrude(context, id + "F27", {"entities" : qUnion([Q0]), "operationType" : NewBodyOperationType.ADD, "depth" : 2.24 * mm, "offsetDistance" : 25 * mm});
        }
        {
            var Q0;
            Q0=makeQuery(id+"F27.opExtrude","CAP_FACE",FACE,{"disambiguationData":[OSD([sQuery(id+"F26.wireOp",EDGE,"E88")])],"isStart":false});
            var sketch = newSketch(context, id + "F28", { "sketchPlane" : qUnion([Q0])});
            skLineSegment(sketch, "E89.bottom", {"start": v(-12.44, 2.84) * mm, "end": v(-7.72, 2.84) * mm});
            skLineSegment(sketch, "E89.top", {"start": v(-12.44, -1.23) * mm, "end": v(-7.72, -1.23) * mm});
            skLineSegment(sketch, "E89.left", {"start": v(-12.44, 2.84) * mm, "end": v(-12.44, -1.23) * mm});
            skLineSegment(sketch, "E89.right", {"start": v(-7.72, 2.84) * mm, "end": v(-7.72, -1.23) * mm});
            skSolve(sketch);
        }
        {
            var Q0;
            Q0=makeQuery(id+"F28.imprint","IMPRINT",FACE,{"disambiguationData":[TD([[makeQuery(id+"F28.imprint","IMPRINT",EDGE,{"derivedFrom":sQuery(id+"F28.wireOp",EDGE,"E89.bottom")}),-1.0]])]});
            extrude(context, id + "F29", {"entities" : qUnion([Q0]), "depth" : 4.6 * mm, "offsetDistance" : 25 * mm});
        }
        {
            var Q0;
            Q0=makeQuery(id+"F29.opExtrude","SWEPT_BODY",BODY,{"disambiguationData":[OSD([sQuery(id+"F26.wireOp",EDGE,"E88"),sQuery(id+"F28.wireOp",EDGE,"E89.bottom"),sQuery(id+"F28.wireOp",EDGE,"E89.top"),sQuery(id+"F28.wireOp",EDGE,"E89.left"),sQuery(id+"F28.wireOp",EDGE,"E89.right")])]});
            deleteBodies(context, id + "F30", {"entities" : qUnion([Q0])});
        }
        {
            var Q0;
            Q0=makeQuery(id+"F27.opExtrude","CAP_FACE",FACE,{"disambiguationData":[OSD([sQuery(id+"F26.wireOp",EDGE,"E88")])],"isStart":false});
            var sketch = newSketch(context, id + "F31", { "sketchPlane" : qUnion([Q0])});
            skLineSegment(sketch, "E90.bottom", {"start": v(-7.86, -1.13) * mm, "end": v(-12.5, -1.13) * mm});
            skLineSegment(sketch, "E90.top", {"start": v(-7.86, 3.12) * mm, "end": v(-12.5, 3.12) * mm});
            skLineSegment(sketch, "E90.left", {"start": v(-7.86, -1.13) * mm, "end": v(-7.86, 3.12) * mm});
            skLineSegment(sketch, "E90.right", {"start": v(-12.5, -1.13) * mm, "end": v(-12.5, 3.12) * mm});
            skSolve(sketch);
        }
        {
            var Q0;
            Q0=makeQuery(id+"F31.imprint","IMPRINT",FACE,{"disambiguationData":[TD([[makeQuery(id+"F31.imprint","IMPRINT",EDGE,{"derivedFrom":sQuery(id+"F31.wireOp",EDGE,"E90.bottom")}),-1.0]])]});
            var Q1;
            Q1=makeQuery(id+"F31.imprint","IMPRINT",FACE,{"disambiguationData":[TD([[makeQuery(id+"F31.imprint","IMPRINT",EDGE,{"derivedFrom":makeQuery(id+"F27.opExtrude","CAP_EDGE",EDGE,{"disambiguationData":[OSD([sQuery(id+"F26.wireOp",EDGE,"E88")])],"isStart":false})}),1.0]])]});
            extrude(context, id + "F32", {"entities" : qUnion([Q0, Q1]), "operationType" : NewBodyOperationType.ADD, "depth" : 5.1 * mm, "offsetDistance" : 25 * mm});
        }
        {
            var Q0;
            Q0=makeQuery(id+"F32.opExtrude","SWEPT_FACE",FACE,{"disambiguationData":[OSD([sQuery(id+"F31.wireOp",EDGE,"E90.bottom")])]});
            var sketch = newSketch(context, id + "F33", { "sketchPlane" : qUnion([Q0])});
            skCircle(sketch, "E91", {"center": v(10.53, -1.93) * mm, "radius": 1.54 * mm});
            skCircle(sketch, "E92", {"center": v(10.53, -1.93) * mm, "radius": 2.5 * mm});
            skFitSpline(sketch, "E93", {"points": [v(9.3, -2.86) * mm, v(9.49, -3.57) * mm, v(9.21, -4.06) * mm], "startDerivative": vector(0.62, -1.42) * mm, "endDerivative": vector(-0.81, -0.98) * mm});
            skFitSpline(sketch, "E94", {"points": [v(12.03, -2.29) * mm, v(12.13, -3.25) * mm, v(12.55, -3.42) * mm], "startDerivative": vector(-0.1, -1.98) * mm, "endDerivative": vector(1.21, -0.16) * mm});
            skSolve(sketch);
        }
        {
            var Q0;
            {var subQ0=sQuery(id+"F33.wireOp",EDGE,"E91");var subQ1=makeQuery(id+"F33.imprint","INTERSECT",VERTEX,{"derivedFrom":[subQ0,sQuery(id+"F33.wireOp",EDGE,"E93")]});Q0=makeQuery(id+"F33.imprint","IMPRINT",FACE,{"disambiguationData":[TD([[makeQuery(id+"F33.imprint","IMPRINT",EDGE,{"disambiguationData":[TD([[subQ1,-1.0]])],"derivedFrom":subQ0}),1.0]])]});}
            var Q1;
            {var subQ0=sQuery(id+"F33.wireOp",EDGE,"E93");Q1=makeQuery(id+"F33.imprint","IMPRINT",FACE,{"disambiguationData":[TD([[makeQuery(id+"F33.imprint","IMPRINT",EDGE,{"derivedFrom":subQ0}),1.0]])]});}
            var Q2;
            {var subQ2=sQuery(id+"F31.wireOp",EDGE,"E90.bottom");var subQ6=makeQuery(id+"F32.opExtrude","CAP_EDGE",EDGE,{"disambiguationData":[OSD([subQ2])],"isStart":false});Q2=makeQuery(id+"F33.imprint","IMPRINT",FACE,{"disambiguationData":[TD([[makeQuery(id+"F33.imprint","IMPRINT",EDGE,{"derivedFrom":subQ6}),1.0]])]});}
            var Q3;
            {var subQ0=sQuery(id+"F33.wireOp",EDGE,"E92");var subQ1=sQuery(id+"F31.wireOp",EDGE,"E90.bottom");var subQ4=makeQuery(id+"F32.opExtrude","CAP_EDGE",EDGE,{"disambiguationData":[OSD([subQ1])],"isStart":true});var subQ5=makeQuery(id+"F33.imprint","INTERSECT",VERTEX,{"disambiguationData":[OD(0.0)],"derivedFrom":[subQ4,subQ0]});Q3=makeQuery(id+"F33.imprint","IMPRINT",FACE,{"disambiguationData":[TD([[makeQuery(id+"F33.imprint","IMPRINT",EDGE,{"disambiguationData":[TD([[subQ5,1.0]])],"derivedFrom":subQ0}),-1.0]])]});}
            var Q4;
            {var subQ0=sQuery(id+"F33.wireOp",EDGE,"E92");var subQ1=sQuery(id+"F31.wireOp",EDGE,"E90.bottom");var subQ2=makeQuery(id+"F32.opExtrude","CAP_EDGE",EDGE,{"disambiguationData":[OSD([subQ1])],"isStart":true});var subQ3=makeQuery(id+"F33.imprint","INTERSECT",VERTEX,{"disambiguationData":[OD(1.0)],"derivedFrom":[subQ2,subQ0]});Q4=makeQuery(id+"F33.imprint","IMPRINT",FACE,{"disambiguationData":[TD([[makeQuery(id+"F33.imprint","IMPRINT",EDGE,{"disambiguationData":[TD([[subQ3,-1.0]])],"derivedFrom":subQ0}),-1.0]])]});}
            extrude(context, id + "F34", {"entities" : qUnion([Q0, Q1, Q2, Q3, Q4]), "operationType" : NewBodyOperationType.REMOVE, "oppositeDirection" : true, "depth" : 25 * mm, "offsetDistance" : 25 * mm});
        }
    });
